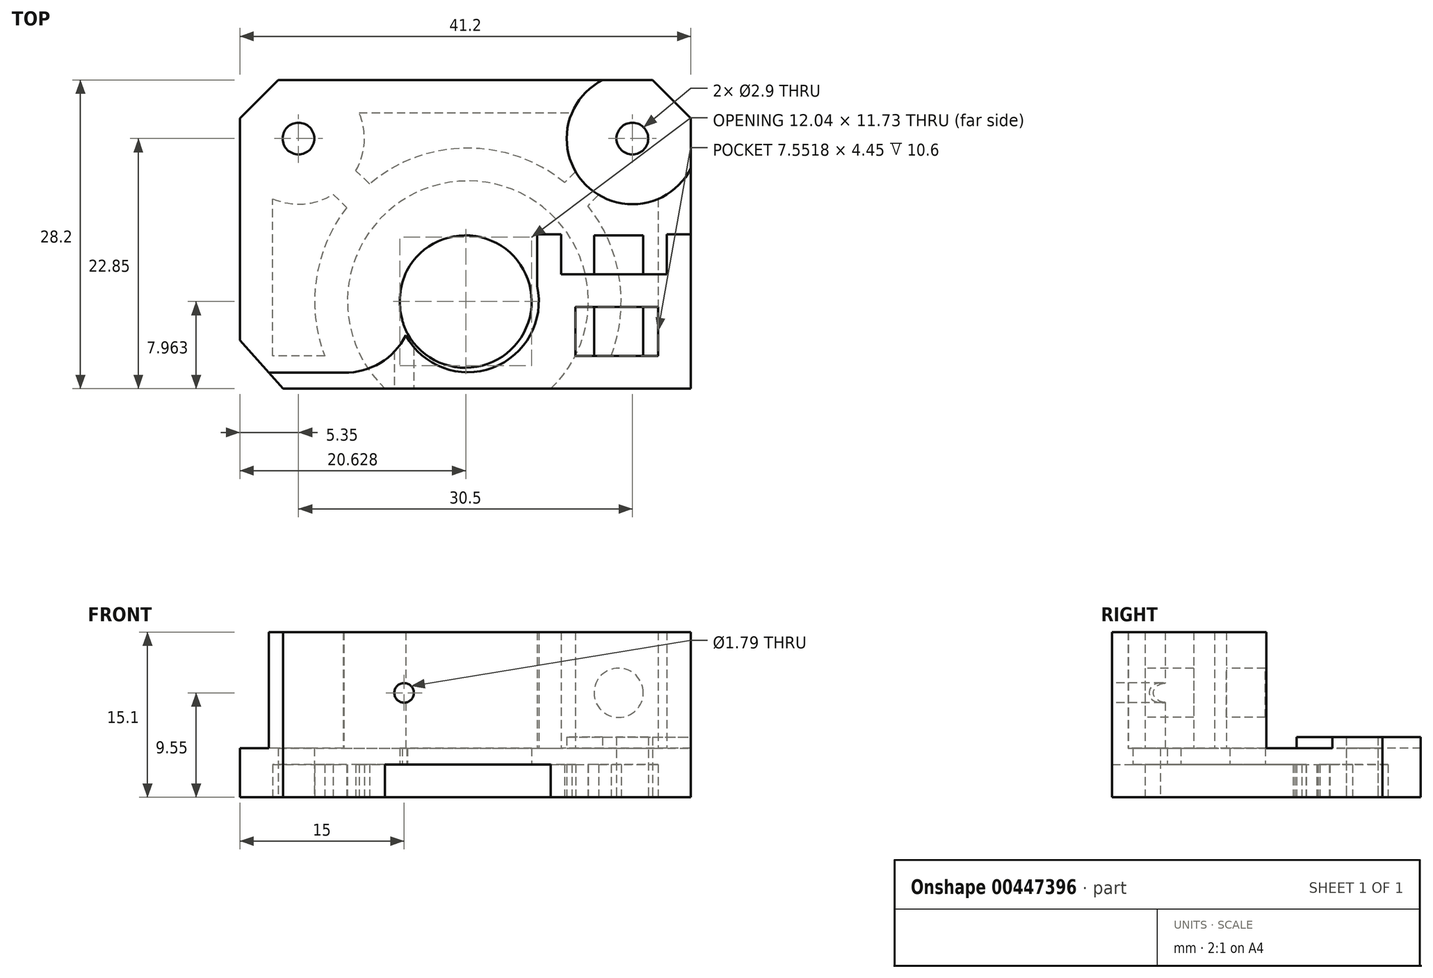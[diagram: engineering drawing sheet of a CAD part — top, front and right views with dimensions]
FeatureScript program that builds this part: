
annotation { "Feature Type Name" : "Feature", "Feature Type Description" : "" }
export const myFeature = defineFeature(function(context is Context, id is Id, definition is map)
    precondition{}
    {
        {
            var Q0;
            Q0=qCreatedBy(makeId("Top.planeOp"),FACE);
            var sketch = newSketch(context, id + "F0", { "sketchPlane" : qUnion([Q0])});
            skLineSegment(sketch, "E0.bottom", {"start": v(3.95, 0) * mm, "end": v(41.2, 0) * mm});
            skLineSegment(sketch, "E0.top", {"start": v(3.5, 28.2) * mm, "end": v(37.7, 28.2) * mm});
            skLineSegment(sketch, "E0.right", {"start": v(41.2, 0) * mm, "end": v(41.2, 24.7) * mm});
            skArc(sketch, "E1", {"start": v(6.02, 2.6) * mm, "mid": v(11.23, 2.02) * mm, "end": v(15.04, 5.6) * mm});
            skCircle(sketch, "E2", {"center": v(9.25, 7.95) * mm, "radius": 1.44 * mm});
            skCircle(sketch, "E3", {"center": v(5.35, 22.85) * mm, "radius": 1.45 * mm});
            skCircle(sketch, "E4", {"center": v(35.85, 22.85) * mm, "radius": 1.45 * mm});
            skArc(sketch, "E5", {"start": v(15.3, 5.04) * mm, "mid": v(26.65, 8) * mm, "end": v(15.25, 10.77) * mm});
            skPoint(sketch, "E6.orphan", {"position": v(20.6, 28.2) * mm});
            skLineSegment(sketch, "E7", {"start": v(39, 10.45) * mm, "end": v(29.35, 10.45) * mm});
            skLineSegment(sketch, "E8", {"start": v(9.43, 1.45) * mm, "end": v(2.65, 1.45) * mm});
            skArc(sketch, "E9.trimOffspring", {"start": v(15.25, 10.77) * mm, "mid": v(14.63, 8.56) * mm, "end": v(14.82, 6.28) * mm});
            skLineSegment(sketch, "E10.bottom", {"start": v(41.2, 14.1) * mm, "end": v(39, 14.1) * mm});
            skLineSegment(sketch, "E10.left", {"start": v(41.2, 14.1) * mm, "end": v(41.2, 10.45) * mm});
            skLineSegment(sketch, "E10.right", {"start": v(39, 14.1) * mm, "end": v(39, 10.45) * mm});
            skLineSegment(sketch, "E11.top", {"start": v(27.15, 14.1) * mm, "end": v(29.35, 14.1) * mm});
            skLineSegment(sketch, "E11.left", {"start": v(27.15, 10.45) * mm, "end": v(27.15, 14.1) * mm});
            skLineSegment(sketch, "E11.right", {"start": v(29.35, 10.45) * mm, "end": v(29.35, 14.1) * mm});
            skLineSegment(sketch, "E12", {"start": v(3.95, 0) * mm, "end": v(0, 4.4) * mm});
            skLineSegment(sketch, "E13.trimOffspring", {"start": v(0, 4.4) * mm, "end": v(0, 24.7) * mm});
            skLineSegment(sketch, "E14", {"start": v(3.5, 28.2) * mm, "end": v(0, 24.7) * mm});
            skLineSegment(sketch, "E15", {"start": v(37.7, 28.2) * mm, "end": v(41.2, 24.7) * mm});
            skPoint(sketch, "E16.orphan", {"position": v(0, 28.2) * mm});
            skPoint(sketch, "E17.orphan", {"position": v(41.2, 28.2) * mm});
            skLineSegment(sketch, "E18.bottom", {"start": v(30.65, 7.45) * mm, "end": v(38.2, 7.45) * mm});
            skLineSegment(sketch, "E18.top", {"start": v(30.65, 3) * mm, "end": v(38.2, 3) * mm});
            skLineSegment(sketch, "E18.left", {"start": v(30.65, 7.45) * mm, "end": v(30.65, 3) * mm});
            skLineSegment(sketch, "E18.right", {"start": v(38.2, 7.45) * mm, "end": v(38.2, 3) * mm});
            skArc(sketch, "E19", {"start": v(33.13, 28.2) * mm, "mid": v(31.6, 18.6) * mm, "end": v(41.2, 20.13) * mm});
            skArc(sketch, "E20", {"start": v(0, 20.13) * mm, "mid": v(9.6, 18.6) * mm, "end": v(8.07, 28.2) * mm});
            skLineSegment(sketch, "E21.top", {"start": v(14.82, 6.28) * mm, "end": v(14.83, 6.28) * mm});
            skArc(sketch, "E22", {"start": v(14.83, 6.28) * mm, "mid": v(15.03, 5.65) * mm, "end": v(15.3, 5.04) * mm});
            skArc(sketch, "E23", {"start": v(15.15, 4.86) * mm, "mid": v(23.1, 1.9) * mm, "end": v(27.15, 9.36) * mm});
            skLineSegment(sketch, "E24", {"start": v(27.15, 10.45) * mm, "end": v(27.15, 9.36) * mm});
            skArc(sketch, "E25.trimOffspring", {"start": v(13.68, 12.36) * mm, "mid": v(4.73, 11.5) * mm, "end": v(6.02, 2.6) * mm});
            skArc(sketch, "E26.trimOffspring", {"start": v(9.5, 1.46) * mm, "mid": v(12.82, 2.35) * mm, "end": v(15.15, 4.86) * mm});
            skArc(sketch, "E27.trimOffspring", {"start": v(15.04, 10.3) * mm, "mid": v(14.46, 11.4) * mm, "end": v(13.68, 12.36) * mm});
            skLineSegment(sketch, "E28", {"start": v(9.5, 1.46) * mm, "end": v(9.43, 1.45) * mm});
            skSolve(sketch);
        }
        {
            var Q0;
            {var subQ0=sQuery(id+"F0.wireOp",EDGE,"E0.bottom");Q0=makeQuery(id+"F0.imprint","IMPRINT",FACE,{"disambiguationData":[TD([[makeQuery(id+"F0.imprint","IMPRINT",EDGE,{"derivedFrom":subQ0}),1.0]])]});}
            extrude(context, id + "F1", {"entities" : qUnion([Q0]), "depth" : 15.1 * mm});
        }
        {
            var Q0;
            {var subQ9=sQuery(id+"F0.wireOp",EDGE,"E1");Q0=makeQuery(id+"F0.imprint","IMPRINT",FACE,{"disambiguationData":[TD([[makeQuery(id+"F0.imprint","IMPRINT",EDGE,{"derivedFrom":subQ9}),-1.0]])]});}
            var Q1;
            Q1=makeQuery(id+"F0.imprint","IMPRINT",FACE,{"disambiguationData":[TD([[makeQuery(id+"F0.imprint","IMPRINT",EDGE,{"derivedFrom":sQuery(id+"F0.wireOp",EDGE,"E3")}),-1.0]])]});
            var Q2;
            {var subQ3=sQuery(id+"F0.wireOp",EDGE,"E1");Q2=makeQuery(id+"F0.imprint","IMPRINT",FACE,{"disambiguationData":[TD([[makeQuery(id+"F0.imprint","IMPRINT",EDGE,{"derivedFrom":subQ3}),1.0]])]});}
            var Q3;
            Q3=makeQuery(id+"F0.imprint","IMPRINT",FACE,{"disambiguationData":[TD([[makeQuery(id+"F0.imprint","IMPRINT",EDGE,{"derivedFrom":sQuery(id+"F0.wireOp",EDGE,"E2")}),1.0]])]});
            var Q4;
            Q4=makeQuery(id+"F0.imprint","IMPRINT",FACE,{"disambiguationData":[TD([[makeQuery(id+"F0.imprint","IMPRINT",EDGE,{"derivedFrom":sQuery(id+"F0.wireOp",EDGE,"E18.bottom")}),-1.0]])]});
            extrude(context, id + "F2", {"entities" : qUnion([Q0, Q1, Q2, Q3, Q4]), "operationType" : NewBodyOperationType.ADD, "depth" : 4.5 * mm});
        }
        {
            var Q0;
            Q0=makeQuery(id+"F0.imprint","IMPRINT",FACE,{"disambiguationData":[TD([[makeQuery(id+"F0.imprint","IMPRINT",EDGE,{"derivedFrom":sQuery(id+"F0.wireOp",EDGE,"E4")}),-1.0]])]});
            extrude(context, id + "F3", {"entities" : qUnion([Q0]), "operationType" : NewBodyOperationType.ADD, "depth" : 5.5 * mm});
        }
        {
            var Q0;
            Q0=qCreatedBy(makeId("Top.planeOp"),FACE);
            var sketch = newSketch(context, id + "F4", { "sketchPlane" : qUnion([Q0])});
            skCircle(sketch, "E29", {"center": v(20.83, 7.98) * mm, "radius": 11 * mm});
            skArc(sketch, "E30", {"start": v(3, 17.34) * mm, "mid": v(5.8, 16.87) * mm, "end": v(8.51, 17.75) * mm});
            skArc(sketch, "E31", {"start": v(30.33, 25.2) * mm, "mid": v(29.86, 22.48) * mm, "end": v(30.67, 19.84) * mm});
            skLineSegment(sketch, "E32", {"start": v(7.74, 3) * mm, "end": v(3, 3) * mm});
            skLineSegment(sketch, "E33", {"start": v(3, 3) * mm, "end": v(3, 17.34) * mm});
            skLineSegment(sketch, "E34", {"start": v(10.9, 25.2) * mm, "end": v(30.33, 25.2) * mm});
            skLineSegment(sketch, "E35", {"start": v(38.2, 17.34) * mm, "end": v(38.2, 3) * mm});
            skLineSegment(sketch, "E36", {"start": v(38.2, 3) * mm, "end": v(33.91, 3) * mm});
            skLineSegment(sketch, "E37", {"start": v(8.51, 17.75) * mm, "end": v(9.76, 16.55) * mm});
            skLineSegment(sketch, "E38", {"start": v(11.84, 18.71) * mm, "end": v(10.6, 19.91) * mm});
            skLineSegment(sketch, "E39", {"start": v(30.67, 19.84) * mm, "end": v(29.66, 18.84) * mm});
            skLineSegment(sketch, "E40", {"start": v(32.78, 17.7) * mm, "end": v(31.77, 16.7) * mm});
            skPoint(sketch, "E41.orphan", {"position": v(38.2, 0) * mm});
            skArc(sketch, "E42", {"start": v(33.91, 3) * mm, "mid": v(34.66, 10.14) * mm, "end": v(31.77, 16.7) * mm});
            skArc(sketch, "E43.trimOffspring", {"start": v(29.66, 18.84) * mm, "mid": v(20.73, 21.98) * mm, "end": v(11.84, 18.71) * mm});
            skArc(sketch, "E44.trimOffspring", {"start": v(32.78, 17.7) * mm, "mid": v(35.45, 16.87) * mm, "end": v(38.2, 17.34) * mm});
            skArc(sketch, "E45.trimOffspring", {"start": v(10.6, 19.91) * mm, "mid": v(11.36, 22.52) * mm, "end": v(10.9, 25.2) * mm});
            skArc(sketch, "E46.trimOffspring", {"start": v(9.76, 16.55) * mm, "mid": v(6.98, 10.04) * mm, "end": v(7.74, 3) * mm});
            skSolve(sketch);
        }
        {
            var Q0;
            Q0=makeQuery(id+"F4.imprint","IMPRINT",FACE,{"disambiguationData":[TD([[makeQuery(id+"F4.imprint","IMPRINT",EDGE,{"derivedFrom":sQuery(id+"F4.wireOp",EDGE,"E30")}),-1.0]])]});
            var Q1;
            Q1=makeQuery(id+"F4.imprint","IMPRINT",FACE,{"disambiguationData":[TD([[makeQuery(id+"F4.imprint","IMPRINT",EDGE,{"derivedFrom":sQuery(id+"F4.wireOp",EDGE,"E29")}),1.0]])]});
            var Q2;
            Q2=makeQuery(id+"F4.imprint","IMPRINT",FACE,{"disambiguationData":[TD([[makeQuery(id+"F4.imprint","IMPRINT",EDGE,{"derivedFrom":sQuery(id+"F4.wireOp",EDGE,"E35")}),-1.0]])]});
            var Q3;
            Q3=makeQuery(id+"F4.imprint","IMPRINT",FACE,{"disambiguationData":[TD([[makeQuery(id+"F4.imprint","IMPRINT",EDGE,{"derivedFrom":sQuery(id+"F4.wireOp",EDGE,"E31")}),-1.0]])]});
            extrude(context, id + "F5", {"entities" : qUnion([Q0, Q1, Q2, Q3]), "operationType" : NewBodyOperationType.REMOVE, "depth" : 3 * mm});
        }
        {
            var Q0;
            Q0=qCreatedBy(makeId("Front.planeOp"),FACE);
            var sketch = newSketch(context, id + "F6", { "sketchPlane" : qUnion([Q0])});
            skCircle(sketch, "E47", {"center": v(15, 9.55) * mm, "radius": 1 * mm});
            skCircle(sketch, "E48", {"center": v(34.6, 9.55) * mm, "radius": 2.25 * mm});
            skSolve(sketch);
        }
        {
            var Q0;
            Q0=makeQuery(id+"F6.imprint","IMPRINT",FACE,{"disambiguationData":[TD([[makeQuery(id+"F6.imprint","IMPRINT",EDGE,{"derivedFrom":sQuery(id+"F6.wireOp",EDGE,"E48")}),1.0]])]});
            var Q1;
            Q1=sQuery(id+"F6.wireOp",EDGE,"E48");
            extrude(context, id + "F7", {"entities" : qUnion([Q0]), "operationType" : NewBodyOperationType.ADD, "surfaceEntities" : qUnion([Q1]), "oppositeDirection" : true, "depth" : 14 * mm});
        }
        {
            var Q0;
            Q0=sQuery(id+"F6.wireOp",VERTEX,"E47.center");
            var Q1;
            Q1=makeQuery(id+"F1.opExtrude","SWEPT_BODY",BODY,{"disambiguationData":[OSD([sQuery(id+"F0.wireOp",EDGE,"E0.bottom"),sQuery(id+"F0.wireOp",EDGE,"E0.right"),sQuery(id+"F0.wireOp",EDGE,"E7"),sQuery(id+"F0.wireOp",EDGE,"E8"),sQuery(id+"F0.wireOp",EDGE,"E10.bottom"),sQuery(id+"F0.wireOp",EDGE,"E10.left"),sQuery(id+"F0.wireOp",EDGE,"E10.right"),sQuery(id+"F0.wireOp",EDGE,"E11.top"),sQuery(id+"F0.wireOp",EDGE,"E11.left"),sQuery(id+"F0.wireOp",EDGE,"E11.right"),sQuery(id+"F0.wireOp",EDGE,"E12"),sQuery(id+"F0.wireOp",EDGE,"E18.bottom"),sQuery(id+"F0.wireOp",EDGE,"E18.top"),sQuery(id+"F0.wireOp",EDGE,"E18.left"),sQuery(id+"F0.wireOp",EDGE,"E18.right"),sQuery(id+"F0.wireOp",EDGE,"E23"),sQuery(id+"F0.wireOp",EDGE,"E24"),sQuery(id+"F0.wireOp",EDGE,"E26.trimOffspring"),sQuery(id+"F0.wireOp",EDGE,"E28")])]});
            hole(context, id + "F8", {"style" : HoleStyle.C_BORE, "endStyle" : HoleEndStyle.THROUGH, "holeDiameter" : 1.79 * mm, "cBoreDiameter" : 1.79 * mm, "cBoreDepth" : 1.45 * mm, "isTappedThrough" : true, "tappedDepth" : 12 * mm, "tapClearance" : 3, "locations" : qUnion([Q0]), "scope" : qUnion([Q1])});
        }
    });
